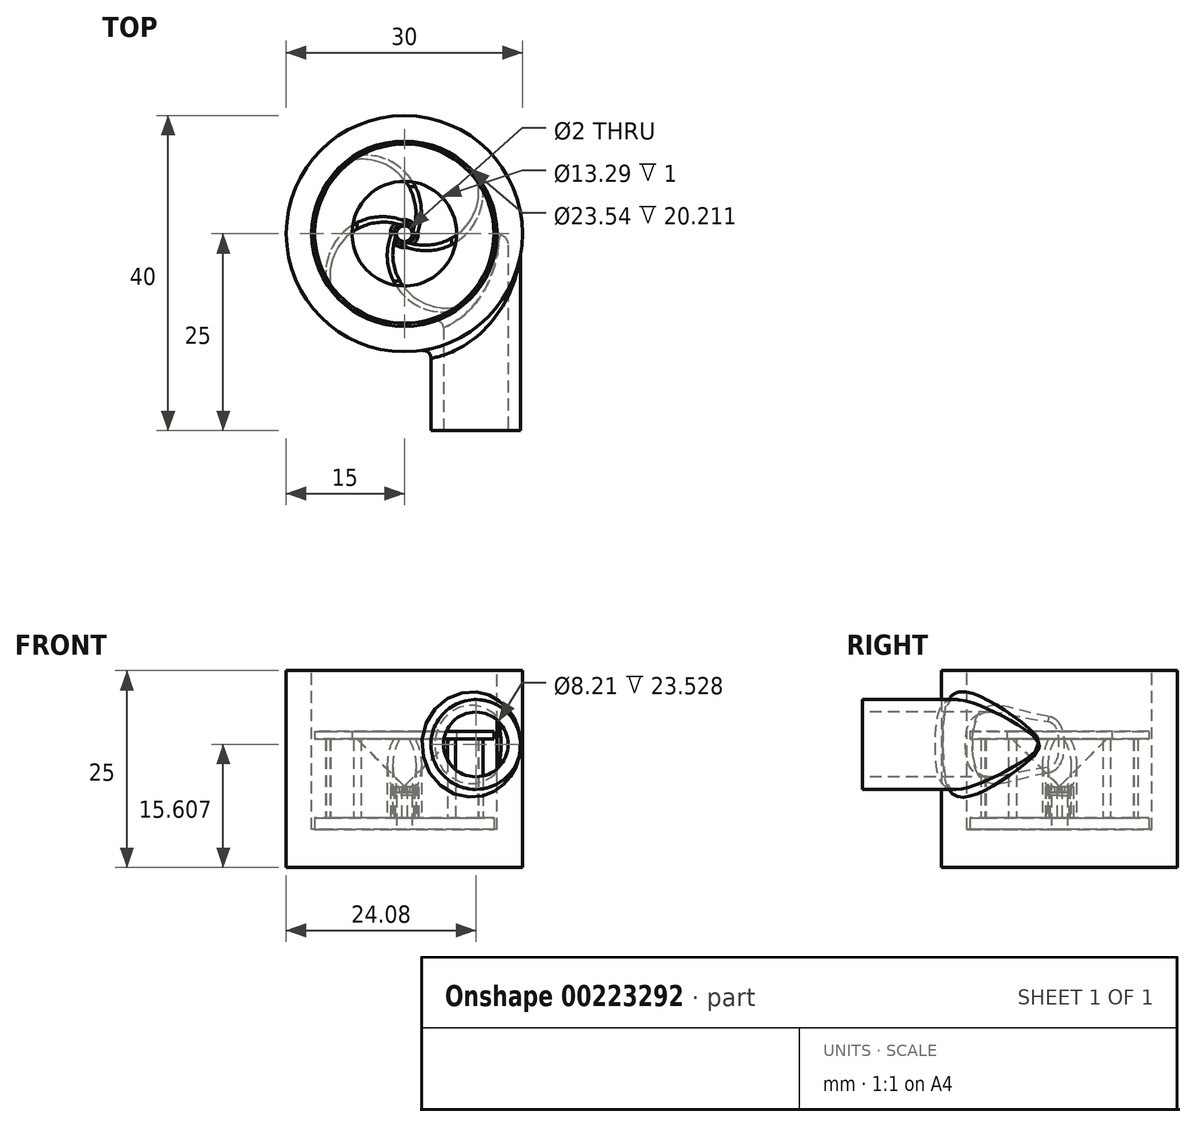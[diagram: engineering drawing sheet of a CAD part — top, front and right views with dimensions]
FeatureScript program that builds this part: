
annotation { "Feature Type Name" : "Feature", "Feature Type Description" : "" }
export const myFeature = defineFeature(function(context is Context, id is Id, definition is map)
    precondition{}
    {
        {
            var Q0;
            Q0=qCreatedBy(makeId("Top.planeOp"),FACE);
            var sketch = newSketch(context, id + "F0", { "sketchPlane" : qUnion([Q0])});
            skCircle(sketch, "E0", {"center": v(0, 0) * mm, "radius": 15 * mm});
            skSolve(sketch);
        }
        {
            var Q0;
            Q0 = qSketchRegion(id + "F0", true);
            extrude(context, id + "F1", {"entities" : qUnion([Q0]), "depth" : 25 * mm});
        }
        {
            var Q0;
            Q0=qCreatedBy(makeId("Front.planeOp"),FACE);
            var sketch = newSketch(context, id + "F2", { "sketchPlane" : qUnion([Q0])});
            skCircle(sketch, "E1", {"center": v(9.08, 15.6) * mm, "radius": 5.7 * mm});
            skSolve(sketch);
        }
        {
            var Q0;
            Q0 = qSketchRegion(id + "F2", true);
            extrude(context, id + "F3", {"entities" : qUnion([Q0]), "operationType" : NewBodyOperationType.ADD, "depth" : 25 * mm});
        }
        {
            var Q0;
            Q0=makeQuery(id+"F1.opExtrude","CAP_FACE",FACE,{"disambiguationData":[OSD([sQuery(id+"F0.wireOp",EDGE,"E0")])],"isStart":false});
            var sketch = newSketch(context, id + "F4", { "sketchPlane" : qUnion([Q0])});
            skCircle(sketch, "E2", {"center": v(0, 0) * mm, "radius": 11.77 * mm});
            skSolve(sketch);
        }
        {
            var Q0;
            Q0=makeQuery(id+"F4.imprint","IMPRINT",FACE,{"disambiguationData":[TD([[makeQuery(id+"F4.imprint","IMPRINT",EDGE,{"derivedFrom":sQuery(id+"F4.wireOp",EDGE,"E2")}),1.0]])]});
            extrude(context, id + "F5", {"entities" : qUnion([Q0]), "operationType" : NewBodyOperationType.REMOVE, "oppositeDirection" : true, "depth" : 20.21 * mm});
        }
        {
            var Q0;
            Q0=makeQuery(id+"F3.opExtrude","CAP_FACE",FACE,{"disambiguationData":[OSD([sQuery(id+"F2.wireOp",EDGE,"E1")])],"isStart":false});
            var sketch = newSketch(context, id + "F6", { "sketchPlane" : qUnion([Q0])});
            skCircle(sketch, "E3", {"center": v(9.08, 15.6) * mm, "radius": 4.1 * mm});
            skSolve(sketch);
        }
        {
            var Q0;
            Q0=makeQuery(id+"F6.imprint","IMPRINT",FACE,{"disambiguationData":[TD([[makeQuery(id+"F6.imprint","IMPRINT",EDGE,{"derivedFrom":sQuery(id+"F6.wireOp",EDGE,"E3")}),1.0]])]});
            extrude(context, id + "F7", {"entities" : qUnion([Q0]), "operationType" : NewBodyOperationType.REMOVE, "oppositeDirection" : true, "depth" : 25 * mm});
        }
        {
            var Q0;
            Q0=makeQuery(id+"F7.boolean.opBoolean","COPY",EDGE,{"derivedFrom":makeQuery(id+"F7.opExtrude","CAP_EDGE",EDGE,{"disambiguationData":[OSD([sQuery(id+"F6.wireOp",EDGE,"E3")])],"isStart":false})});
            fillet(context, id + "F8", {"entities" : qUnion([Q0]), "radius" : 1.47 * mm, "tangentPropagation" : true, "allowEdgeOverflow" : false});
        }
        {
            var Q0;
            Q0=makeQuery(id+"F8.opFillet","BLEND_EDGE",EDGE,{"blendedFrom":[makeQuery(id+"F7.boolean.opBoolean","COPY",EDGE,{"derivedFrom":makeQuery(id+"F7.opExtrude","CAP_EDGE",EDGE,{"disambiguationData":[OSD([sQuery(id+"F6.wireOp",EDGE,"E3")])],"isStart":false})}),makeQuery(id+"F5.boolean.opBoolean","COPY",FACE,{"derivedFrom":makeQuery(id+"F5.opExtrude","SWEPT_FACE",FACE,{"disambiguationData":[OSD([sQuery(id+"F4.wireOp",EDGE,"E2")])]})})],"blendedInto":[makeQuery(id+"F5.boolean.opBoolean","COPY",FACE,{"derivedFrom":makeQuery(id+"F5.opExtrude","SWEPT_FACE",FACE,{"disambiguationData":[OSD([sQuery(id+"F4.wireOp",EDGE,"E2")])]})})]});
            var Q1;
            Q1=makeQuery(id+"F7.boolean.opBoolean","INTERSECT",EDGE,{"derivedFrom":[makeQuery(id+"F5.boolean.opBoolean","COPY",FACE,{"derivedFrom":makeQuery(id+"F5.opExtrude","SWEPT_FACE",FACE,{"disambiguationData":[OSD([sQuery(id+"F4.wireOp",EDGE,"E2")])]})}),makeQuery(id+"F7.opExtrude","SWEPT_FACE",FACE,{"disambiguationData":[OSD([sQuery(id+"F6.wireOp",EDGE,"E3")])]})]});
            fillet(context, id + "F9", {"entities" : qUnion([Q0, Q1]), "radius" : 0.87 * mm, "tangentPropagation" : true, "allowEdgeOverflow" : false});
        }
        {
            var Q0;
            Q0=makeQuery(id+"F3.boolean.opBoolean","INTERSECT",EDGE,{"derivedFrom":[makeQuery(id+"F1.opExtrude","SWEPT_FACE",FACE,{"disambiguationData":[OSD([sQuery(id+"F0.wireOp",EDGE,"E0")])]}),makeQuery(id+"F3.opExtrude","SWEPT_FACE",FACE,{"disambiguationData":[OSD([sQuery(id+"F2.wireOp",EDGE,"E1")])]})]});
            fillet(context, id + "F10", {"entities" : qUnion([Q0]), "radius" : 1 * mm, "tangentPropagation" : true, "allowEdgeOverflow" : false});
        }
        {
            var Q0;
            Q0=makeQuery(id+"F5.boolean.opBoolean","COPY",FACE,{"derivedFrom":makeQuery(id+"F5.opExtrude","CAP_FACE",FACE,{"disambiguationData":[OSD([sQuery(id+"F4.wireOp",EDGE,"E2")])],"isStart":false})});
            var sketch = newSketch(context, id + "F11", { "sketchPlane" : qUnion([Q0])});
            skCircle(sketch, "E4", {"center": v(0, 0) * mm, "radius": 11.38 * mm});
            skSolve(sketch);
        }
        {
            var Q0;
            Q0=makeQuery(id+"F11.imprint","IMPRINT",FACE,{"disambiguationData":[TD([[makeQuery(id+"F11.imprint","IMPRINT",EDGE,{"derivedFrom":sQuery(id+"F11.wireOp",EDGE,"E4")}),1.0]])]});
            extrude(context, id + "F12", {"entities" : qUnion([Q0]), "depth" : 1.5 * mm});
        }
        {
            var Q0;
            Q0=makeQuery(id+"F12.opExtrude","CAP_FACE",FACE,{"disambiguationData":[OSD([sQuery(id+"F11.wireOp",EDGE,"E4")])],"isStart":false});
            var sketch = newSketch(context, id + "F13", { "sketchPlane" : qUnion([Q0])});
            skArc(sketch, "E5", {"start": v(0.95, 0) * mm, "mid": v(-0.01, 6.86) * mm, "end": v(-6.48, 9.36) * mm});
            skLineSegment(sketch, "E6", {"start": v(-6.48, 9.36) * mm, "end": v(-5.5, 9.97) * mm});
            skArc(sketch, "E7", {"start": v(1.62, 0) * mm, "mid": v(0.82, 6.95) * mm, "end": v(-5.5, 9.97) * mm});
            skLineSegment(sketch, "E8", {"start": v(1.62, 0) * mm, "end": v(0.95, 0) * mm});
            skSolve(sketch);
        }
        {
            var Q0;
            Q0 = qSketchRegion(id + "F13", true);
            extrude(context, id + "F14", {"entities" : qUnion([Q0]), "depth" : 10 * mm});
        }
        {
            var Q0;
            Q0=makeQuery(id+"F14.opExtrude","SWEPT_BODY",BODY,{"disambiguationData":[OSD([sQuery(id+"F13.wireOp",EDGE,"E5"),sQuery(id+"F13.wireOp",EDGE,"E6"),sQuery(id+"F13.wireOp",EDGE,"E7"),sQuery(id+"F13.wireOp",EDGE,"E8")])]});
            var Q1;
            Q1=makeQuery(id+"F12.opExtrude","CAP_EDGE",EDGE,{"disambiguationData":[OSD([sQuery(id+"F11.wireOp",EDGE,"E4")])],"isStart":false});
            circularPattern(context, id + "F15", {"entities" : qUnion([Q0]), "axis" : qUnion([Q1]), "angle" : 360 * degree, "instanceCount" : 4, "equalSpace" : true});
        }
        {
            var Q0;
            Q0=makeQuery(id+"F15.opPattern","COPY",EDGE,{"derivedFrom":makeQuery(id+"F14.opExtrude","CAP_EDGE",EDGE,{"disambiguationData":[OSD([sQuery(id+"F13.wireOp",EDGE,"E8")])],"isStart":false}),"instanceName":"3"});
            var Q1;
            Q1=makeQuery(id+"F15.opPattern","COPY",EDGE,{"derivedFrom":makeQuery(id+"F14.opExtrude","CAP_EDGE",EDGE,{"disambiguationData":[OSD([sQuery(id+"F13.wireOp",EDGE,"E8")])],"isStart":false}),"instanceName":"2"});
            var Q2;
            Q2=makeQuery(id+"F14.opExtrude","CAP_EDGE",EDGE,{"disambiguationData":[OSD([sQuery(id+"F13.wireOp",EDGE,"E8")])],"isStart":false});
            var Q3;
            Q3=makeQuery(id+"F15.opPattern","COPY",EDGE,{"derivedFrom":makeQuery(id+"F14.opExtrude","CAP_EDGE",EDGE,{"disambiguationData":[OSD([sQuery(id+"F13.wireOp",EDGE,"E8")])],"isStart":false}),"instanceName":"1"});
            chamfer(context, id + "F16", {"entities" : qUnion([Q0, Q1, Q2, Q3]), "width" : 6 * mm, "tangentPropagation" : true});
        }
        {
            var Q0;
            Q0=makeQuery(id+"F15.opPattern","COPY",FACE,{"derivedFrom":makeQuery(id+"F14.opExtrude","CAP_FACE",FACE,{"disambiguationData":[OSD([sQuery(id+"F13.wireOp",EDGE,"E5"),sQuery(id+"F13.wireOp",EDGE,"E6"),sQuery(id+"F13.wireOp",EDGE,"E7"),sQuery(id+"F13.wireOp",EDGE,"E8")])],"isStart":false}),"instanceName":"2"});
            var sketch = newSketch(context, id + "F17", { "sketchPlane" : qUnion([Q0])});
            skCircle(sketch, "E9", {"center": v(0, 0) * mm, "radius": 6.64 * mm});
            skCircle(sketch, "E10", {"center": v(0, 0) * mm, "radius": 11.38 * mm});
            skSolve(sketch);
        }
        {
            var Q0;
            Q0 = qSketchRegion(id + "F17", true);
            extrude(context, id + "F18", {"entities" : qUnion([Q0]), "depth" : 1 * mm});
        }
        {
            var Q0;
            Q0=makeQuery(id+"F12.opExtrude","CAP_FACE",FACE,{"disambiguationData":[OSD([sQuery(id+"F11.wireOp",EDGE,"E4")])],"isStart":false});
            var sketch = newSketch(context, id + "F19", { "sketchPlane" : qUnion([Q0])});
            skCircle(sketch, "E11", {"center": v(0, 0) * mm, "radius": 1.78 * mm});
            skSolve(sketch);
        }
        {
            var Q0;
            Q0 = qSketchRegion(id + "F19", true);
            extrude(context, id + "F20", {"entities" : qUnion([Q0]), "depth" : 3.9 * mm});
        }
        {
            var Q0;
            Q0=makeQuery(id+"F20.opExtrude","CAP_FACE",FACE,{"disambiguationData":[OSD([sQuery(id+"F19.wireOp",EDGE,"E11")])],"isStart":false});
            var sketch = newSketch(context, id + "F21", { "sketchPlane" : qUnion([Q0])});
            skCircle(sketch, "E12", {"center": v(0, 0) * mm, "radius": 0.67 * mm});
            skCircle(sketch, "E13", {"center": v(0, 0) * mm, "radius": 1.35 * mm});
            skSolve(sketch);
        }
        {
            var Q0;
            Q0=makeQuery(id+"F21.imprint","IMPRINT",FACE,{"disambiguationData":[TD([[makeQuery(id+"F21.imprint","IMPRINT",EDGE,{"derivedFrom":sQuery(id+"F21.wireOp",EDGE,"E12")}),-1.0]])]});
            var Q1;
            Q1=makeQuery(id+"F21.imprint","IMPRINT",FACE,{"disambiguationData":[TD([[makeQuery(id+"F21.imprint","IMPRINT",EDGE,{"derivedFrom":sQuery(id+"F21.wireOp",EDGE,"E12")}),1.0]])]});
            extrude(context, id + "F22", {"entities" : qUnion([Q0, Q1]), "operationType" : NewBodyOperationType.REMOVE, "oppositeDirection" : true, "depth" : 2 * mm});
        }
        {
            var Q0;
            Q0=makeQuery(id+"F22.boolean.opBoolean","COPY",EDGE,{"derivedFrom":makeQuery(id+"F22.opExtrude","CAP_EDGE",EDGE,{"disambiguationData":[OSD([sQuery(id+"F21.wireOp",EDGE,"E13")])],"isStart":false})});
            chamfer(context, id + "F23", {"entities" : qUnion([Q0]), "width" : 1.3 * mm, "tangentPropagation" : true});
        }
        {
            var Q0;
            Q0=makeQuery(id+"F22.boolean.opBoolean","COPY",EDGE,{"derivedFrom":makeQuery(id+"F22.opExtrude","CAP_EDGE",EDGE,{"disambiguationData":[OSD([sQuery(id+"F21.wireOp",EDGE,"E13")])],"isStart":true})});
            chamfer(context, id + "F24", {"entities" : qUnion([Q0]), "width" : .7 * mm, "tangentPropagation" : true});
        }
        {
            var Q0;
            Q0=makeQuery(id+"F12.opExtrude","CAP_FACE",FACE,{"disambiguationData":[OSD([sQuery(id+"F11.wireOp",EDGE,"E4")])],"isStart":true});
            var sketch = newSketch(context, id + "F25", { "sketchPlane" : qUnion([Q0])});
            skCircle(sketch, "E14", {"center": v(0, 0) * mm, "radius": 1 * mm});
            skSolve(sketch);
        }
        {
            var Q0;
            Q0 = qSketchRegion(id + "F25", true);
            extrude(context, id + "F26", {"entities" : qUnion([Q0]), "operationType" : NewBodyOperationType.REMOVE, "oppositeDirection" : true, "depth" : 33.4 * mm});
        }
        {
            var Q0;
            Q0=makeQuery(id+"F12.opExtrude","SWEPT_BODY",BODY,{"disambiguationData":[OSD([sQuery(id+"F11.wireOp",EDGE,"E4")])]});
            var Q1;
            Q1=makeQuery(id+"F20.opExtrude","SWEPT_BODY",BODY,{"disambiguationData":[OSD([sQuery(id+"F19.wireOp",EDGE,"E11")])]});
            var Q2;
            Q2=makeQuery(id+"F15.opPattern","COPY",BODY,{"derivedFrom":makeQuery(id+"F14.opExtrude","SWEPT_BODY",BODY,{"disambiguationData":[OSD([sQuery(id+"F13.wireOp",EDGE,"E5"),sQuery(id+"F13.wireOp",EDGE,"E6"),sQuery(id+"F13.wireOp",EDGE,"E7"),sQuery(id+"F13.wireOp",EDGE,"E8")])]}),"instanceName":"2"});
            var Q3;
            Q3=makeQuery(id+"F15.opPattern","COPY",BODY,{"derivedFrom":makeQuery(id+"F14.opExtrude","SWEPT_BODY",BODY,{"disambiguationData":[OSD([sQuery(id+"F13.wireOp",EDGE,"E5"),sQuery(id+"F13.wireOp",EDGE,"E6"),sQuery(id+"F13.wireOp",EDGE,"E7"),sQuery(id+"F13.wireOp",EDGE,"E8")])]}),"instanceName":"3"});
            var Q4;
            Q4=makeQuery(id+"F15.opPattern","COPY",BODY,{"derivedFrom":makeQuery(id+"F14.opExtrude","SWEPT_BODY",BODY,{"disambiguationData":[OSD([sQuery(id+"F13.wireOp",EDGE,"E5"),sQuery(id+"F13.wireOp",EDGE,"E6"),sQuery(id+"F13.wireOp",EDGE,"E7"),sQuery(id+"F13.wireOp",EDGE,"E8")])]}),"instanceName":"1"});
            var Q5;
            Q5=makeQuery(id+"F18.opExtrude","SWEPT_BODY",BODY,{"disambiguationData":[OSD([sQuery(id+"F17.wireOp",EDGE,"E9"),sQuery(id+"F17.wireOp",EDGE,"E10")])]});
            var Q6;
            Q6=makeQuery(id+"F14.opExtrude","SWEPT_BODY",BODY,{"disambiguationData":[OSD([sQuery(id+"F13.wireOp",EDGE,"E5"),sQuery(id+"F13.wireOp",EDGE,"E6"),sQuery(id+"F13.wireOp",EDGE,"E7"),sQuery(id+"F13.wireOp",EDGE,"E8")])]});
            booleanBodies(context, id + "F27", {"operationType" : BooleanOperationType.UNION, "tools" : qUnion([Q0, Q1, Q2, Q3, Q4, Q5, Q6])});
        }
        {
            var Q0;
            Q0=makeQuery(id+"F27.opBoolean","INTERSECT",EDGE,{"derivedFrom":[makeQuery(id+"F15.opPattern","COPY",FACE,{"derivedFrom":makeQuery(id+"F14.opExtrude","SWEPT_FACE",FACE,{"disambiguationData":[OSD([sQuery(id+"F13.wireOp",EDGE,"E5")])]}),"instanceName":"2"}),makeQuery(id+"F23.opChamfer","BLEND_FACE",FACE,{"disambiguationData":[OSD([sQuery(id+"F21.wireOp",EDGE,"E13")])]})]});
            var Q1;
            Q1=makeQuery(id+"F27.opBoolean","INTERSECT",EDGE,{"derivedFrom":[makeQuery(id+"F15.opPattern","COPY",FACE,{"derivedFrom":makeQuery(id+"F14.opExtrude","SWEPT_FACE",FACE,{"disambiguationData":[OSD([sQuery(id+"F13.wireOp",EDGE,"E5")])]}),"instanceName":"3"}),makeQuery(id+"F23.opChamfer","BLEND_FACE",FACE,{"disambiguationData":[OSD([sQuery(id+"F21.wireOp",EDGE,"E13")])]})]});
            var Q2;
            Q2=makeQuery(id+"F27.opBoolean","INTERSECT",EDGE,{"derivedFrom":[makeQuery(id+"F15.opPattern","COPY",FACE,{"derivedFrom":makeQuery(id+"F14.opExtrude","SWEPT_FACE",FACE,{"disambiguationData":[OSD([sQuery(id+"F13.wireOp",EDGE,"E8")])]}),"instanceName":"2"}),makeQuery(id+"F23.opChamfer","BLEND_FACE",FACE,{"disambiguationData":[OSD([sQuery(id+"F21.wireOp",EDGE,"E13")])]})]});
            var Q3;
            Q3=makeQuery(id+"F27.opBoolean","INTERSECT",EDGE,{"derivedFrom":[makeQuery(id+"F15.opPattern","COPY",FACE,{"derivedFrom":makeQuery(id+"F14.opExtrude","SWEPT_FACE",FACE,{"disambiguationData":[OSD([sQuery(id+"F13.wireOp",EDGE,"E8")])]}),"instanceName":"1"}),makeQuery(id+"F23.opChamfer","BLEND_FACE",FACE,{"disambiguationData":[OSD([sQuery(id+"F21.wireOp",EDGE,"E13")])]})]});
            var Q4;
            Q4=makeQuery(id+"F27.opBoolean","INTERSECT",EDGE,{"derivedFrom":[makeQuery(id+"F15.opPattern","COPY",FACE,{"derivedFrom":makeQuery(id+"F14.opExtrude","SWEPT_FACE",FACE,{"disambiguationData":[OSD([sQuery(id+"F13.wireOp",EDGE,"E5")])]}),"instanceName":"1"}),makeQuery(id+"F23.opChamfer","BLEND_FACE",FACE,{"disambiguationData":[OSD([sQuery(id+"F21.wireOp",EDGE,"E13")])]})]});
            var Q5;
            Q5=makeQuery(id+"F27.opBoolean","INTERSECT",EDGE,{"derivedFrom":[makeQuery(id+"F14.opExtrude","SWEPT_FACE",FACE,{"disambiguationData":[OSD([sQuery(id+"F13.wireOp",EDGE,"E5")])]}),makeQuery(id+"F23.opChamfer","BLEND_FACE",FACE,{"disambiguationData":[OSD([sQuery(id+"F21.wireOp",EDGE,"E13")])]})]});
            var Q6;
            Q6=makeQuery(id+"F27.opBoolean","INTERSECT",EDGE,{"derivedFrom":[makeQuery(id+"F14.opExtrude","SWEPT_FACE",FACE,{"disambiguationData":[OSD([sQuery(id+"F13.wireOp",EDGE,"E8")])]}),makeQuery(id+"F23.opChamfer","BLEND_FACE",FACE,{"disambiguationData":[OSD([sQuery(id+"F21.wireOp",EDGE,"E13")])]})]});
            var Q7;
            Q7=makeQuery(id+"F27.opBoolean","INTERSECT",EDGE,{"derivedFrom":[makeQuery(id+"F15.opPattern","COPY",FACE,{"derivedFrom":makeQuery(id+"F14.opExtrude","SWEPT_FACE",FACE,{"disambiguationData":[OSD([sQuery(id+"F13.wireOp",EDGE,"E8")])]}),"instanceName":"3"}),makeQuery(id+"F23.opChamfer","BLEND_FACE",FACE,{"disambiguationData":[OSD([sQuery(id+"F21.wireOp",EDGE,"E13")])]})]});
            var Q8;
            {var subQ0=sQuery(id+"F13.wireOp",EDGE,"E8");Q8=makeQuery(id+"F16.opChamfer","BLEND_EDGE",EDGE,{"blendedFrom":[makeQuery(id+"F15.opPattern","COPY",EDGE,{"derivedFrom":makeQuery(id+"F14.opExtrude","CAP_EDGE",EDGE,{"disambiguationData":[OSD([subQ0])],"isStart":false}),"instanceName":"3"}),makeQuery(id+"F15.opPattern","COPY",FACE,{"derivedFrom":makeQuery(id+"F14.opExtrude","SWEPT_FACE",FACE,{"disambiguationData":[OSD([subQ0])]}),"instanceName":"3"})],"blendedInto":[makeQuery(id+"F15.opPattern","COPY",FACE,{"derivedFrom":makeQuery(id+"F14.opExtrude","SWEPT_FACE",FACE,{"disambiguationData":[OSD([subQ0])]}),"instanceName":"3"})]});}
            var Q9;
            {var subQ0=sQuery(id+"F13.wireOp",EDGE,"E8");Q9=makeQuery(id+"F16.opChamfer","BLEND_EDGE",EDGE,{"blendedFrom":[makeQuery(id+"F14.opExtrude","CAP_EDGE",EDGE,{"disambiguationData":[OSD([subQ0])],"isStart":false}),makeQuery(id+"F14.opExtrude","SWEPT_FACE",FACE,{"disambiguationData":[OSD([subQ0])]})],"blendedInto":[makeQuery(id+"F14.opExtrude","SWEPT_FACE",FACE,{"disambiguationData":[OSD([subQ0])]})]});}
            var Q10;
            Q10=makeQuery(id+"F15.opPattern","COPY",EDGE,{"derivedFrom":makeQuery(id+"F14.opExtrude","SWEPT_EDGE",EDGE,{"disambiguationData":[OSD([sQuery(id+"F13.wireOp",EDGE,"E5"),sQuery(id+"F13.wireOp",EDGE,"E8")])]}),"instanceName":"3"});
            var Q11;
            Q11=makeQuery(id+"F14.opExtrude","SWEPT_EDGE",EDGE,{"disambiguationData":[OSD([sQuery(id+"F13.wireOp",EDGE,"E5"),sQuery(id+"F13.wireOp",EDGE,"E8")])]});
            var Q12;
            Q12=makeQuery(id+"F15.opPattern","COPY",EDGE,{"derivedFrom":makeQuery(id+"F14.opExtrude","SWEPT_EDGE",EDGE,{"disambiguationData":[OSD([sQuery(id+"F13.wireOp",EDGE,"E5"),sQuery(id+"F13.wireOp",EDGE,"E8")])]}),"instanceName":"1"});
            var Q13;
            Q13=makeQuery(id+"F15.opPattern","COPY",EDGE,{"derivedFrom":makeQuery(id+"F14.opExtrude","SWEPT_EDGE",EDGE,{"disambiguationData":[OSD([sQuery(id+"F13.wireOp",EDGE,"E5"),sQuery(id+"F13.wireOp",EDGE,"E8")])]}),"instanceName":"2"});
            chamfer(context, id + "F28", {"entities" : qUnion([Q0, Q1, Q2, Q3, Q4, Q5, Q6, Q7, Q8, Q9, Q10, Q11, Q12, Q13]), "width" : .1 * mm, "tangentPropagation" : true});
        }
    });
